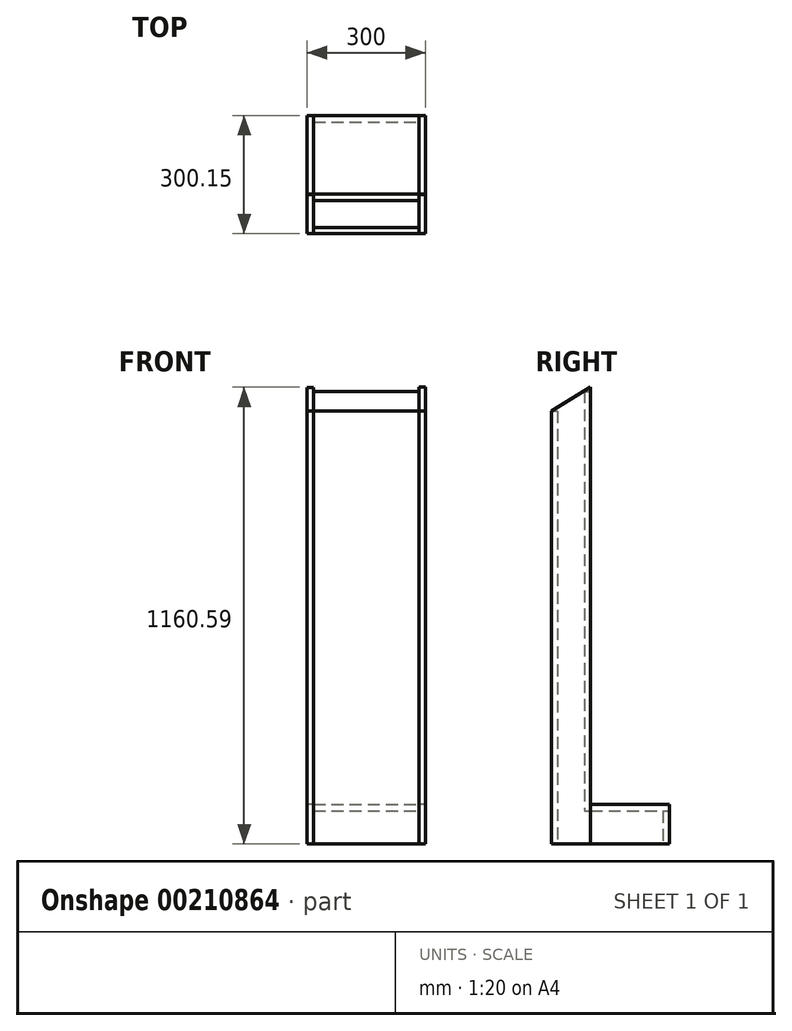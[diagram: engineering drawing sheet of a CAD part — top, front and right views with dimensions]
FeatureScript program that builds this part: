
annotation { "Feature Type Name" : "Feature", "Feature Type Description" : "" }
export const myFeature = defineFeature(function(context is Context, id is Id, definition is map)
    precondition{}
    {
        {
            var Q0;
            Q0=qCreatedBy(makeId("Front.planeOp"),FACE);
            cPlane(context, id + "F0", {"entities" : qUnion([Q0]), "cplaneType" : CPlaneType.OFFSET, "offset" : 100 * mm, "width" : 150 * mm, "height" : 150 * mm});
        }
        {
            var Q0;
            Q0=qCreatedBy(id+"F0.planeOp",FACE);
            var sketch = newSketch(context, id + "F1", { "sketchPlane" : qUnion([Q0])});
            skLineSegment(sketch, "E0.bottom", {"start": v(134, 550) * mm, "end": v(-134, 550) * mm});
            skLineSegment(sketch, "E0.top", {"start": v(134, -550) * mm, "end": v(-134, -550) * mm});
            skLineSegment(sketch, "E0.left", {"start": v(134, 550) * mm, "end": v(134, -550) * mm});
            skLineSegment(sketch, "E0.right", {"start": v(-134, 550) * mm, "end": v(-134, -550) * mm});
            skPoint(sketch, "E0.middle", {"position": v(0, 0) * mm});
            skSolve(sketch);
        }
        {
            var Q0;
            Q0 = qSketchRegion(id + "F1", true);
            extrude(context, id + "F2", {"entities" : qUnion([Q0]), "depth" : 16 * mm});
        }
        {
            var Q0;
            Q0=qCreatedBy(makeId("Front.planeOp"),FACE);
            cPlane(context, id + "F3", {"entities" : qUnion([Q0]), "cplaneType" : CPlaneType.OFFSET, "offset" : 100 * mm, "oppositeDirection" : true, "width" : 150 * mm, "height" : 150 * mm});
        }
        {
            var Q0;
            Q0=qCreatedBy(id+"F3.planeOp",FACE);
            var sketch = newSketch(context, id + "F4", { "sketchPlane" : qUnion([Q0])});
            skLineSegment(sketch, "E1.bottom", {"start": v(-134, 533) * mm, "end": v(134, 533) * mm});
            skLineSegment(sketch, "E1.top", {"start": v(-134, -533) * mm, "end": v(134, -533) * mm});
            skLineSegment(sketch, "E1.left", {"start": v(-134, 533) * mm, "end": v(-134, -533) * mm});
            skLineSegment(sketch, "E1.right", {"start": v(134, 533) * mm, "end": v(134, -533) * mm});
            skPoint(sketch, "E1.middle", {"position": v(0, 0) * mm});
            skSolve(sketch);
        }
        {
            var Q0;
            Q0=makeQuery(id+"F4.imprint","IMPRINT",FACE,{"disambiguationData":[TD([[makeQuery(id+"F4.imprint","IMPRINT",EDGE,{"derivedFrom":sQuery(id+"F4.wireOp",EDGE,"E1.bottom")}),-1.0]])]});
            extrude(context, id + "F5", {"entities" : qUnion([Q0]), "depth" : 16 * mm});
        }
        {
            var Q0;
            Q0=qCreatedBy(makeId("Right.planeOp"),FACE);
            cPlane(context, id + "F6", {"entities" : qUnion([Q0]), "cplaneType" : CPlaneType.OFFSET, "offset" : 100 * mm, "width" : 150 * mm, "height" : 150 * mm});
        }
        {
            var Q0;
            Q0=qCreatedBy(id+"F6.planeOp",FACE);
            var sketch = newSketch(context, id + "F7", { "sketchPlane" : qUnion([Q0])});
            skLineSegment(sketch, "E2.bottom", {"start": v(82.35, 1083.55) * mm, "end": v(-17.65, 1083.55) * mm});
            skLineSegment(sketch, "E2.top", {"start": v(82.35, -76.45) * mm, "end": v(-17.65, -76.45) * mm});
            skLineSegment(sketch, "E2.left", {"start": v(82.35, 1083.55) * mm, "end": v(82.35, -76.45) * mm});
            skLineSegment(sketch, "E2.right", {"start": v(-17.65, 1083.55) * mm, "end": v(-17.65, -76.45) * mm});
            skPoint(sketch, "E2.middle", {"position": v(32.35, 503.55) * mm});
            skSolve(sketch);
        }
        {
            var Q0;
            Q0 = qSketchRegion(id + "F7", true);
            extrude(context, id + "F8", {"entities" : qUnion([Q0]), "depth" : 16 * mm});
        }
        {
            var Q0;
            Q0=qCreatedBy(makeId("Right.planeOp"),FACE);
            cPlane(context, id + "F9", {"entities" : qUnion([Q0]), "cplaneType" : CPlaneType.OFFSET, "offset" : 100 * mm, "oppositeDirection" : true, "width" : 150 * mm, "height" : 150 * mm});
        }
        {
            var Q0;
            Q0=qCreatedBy(id+"F9.planeOp",FACE);
            var sketch = newSketch(context, id + "F10", { "sketchPlane" : qUnion([Q0])});
            skLineSegment(sketch, "E3.bottom", {"start": v(-50, 580) * mm, "end": v(50, 580) * mm});
            skLineSegment(sketch, "E3.top", {"start": v(-50, -580) * mm, "end": v(50, -580) * mm});
            skLineSegment(sketch, "E3.left", {"start": v(-50, 580) * mm, "end": v(-50, -580) * mm});
            skLineSegment(sketch, "E3.right", {"start": v(50, 580) * mm, "end": v(50, -580) * mm});
            skPoint(sketch, "E3.middle", {"position": v(0, 0) * mm});
            skSolve(sketch);
        }
        {
            var Q0;
            Q0=makeQuery(id+"F10.imprint","IMPRINT",FACE,{"disambiguationData":[TD([[makeQuery(id+"F10.imprint","IMPRINT",EDGE,{"derivedFrom":sQuery(id+"F10.wireOp",EDGE,"E3.bottom")}),-1.0]])]});
            extrude(context, id + "F11", {"entities" : qUnion([Q0]), "depth" : 16 * mm});
        }
        {
            var Q0;
            Q0=makeQuery(id+"F2.opExtrude","SWEPT_BODY",BODY,{"disambiguationData":[OSD([sQuery(id+"F1.wireOp",EDGE,"E0.bottom"),sQuery(id+"F1.wireOp",EDGE,"E0.top"),sQuery(id+"F1.wireOp",EDGE,"E0.left"),sQuery(id+"F1.wireOp",EDGE,"E0.right")])]});
            transform(context, id + "F12", {"entities" : qUnion([Q0]), "transformType" : TransformType.TRANSLATION_3D, "dx" : 0 * mm, "dy" : 50 * mm, "dz" : 0 * mm, "makeCopy" : false});
        }
        {
            var Q0;
            Q0=makeQuery(id+"F5.opExtrude","SWEPT_BODY",BODY,{"disambiguationData":[OSD([sQuery(id+"F4.wireOp",EDGE,"E1.bottom"),sQuery(id+"F4.wireOp",EDGE,"E1.top"),sQuery(id+"F4.wireOp",EDGE,"E1.left"),sQuery(id+"F4.wireOp",EDGE,"E1.right")])]});
            transform(context, id + "F13", {"entities" : qUnion([Q0]), "transformType" : TransformType.TRANSLATION_3D, "dx" : 0 * mm, "dy" : -33.8 * mm, "dz" : 0 * mm, "makeCopy" : false});
        }
        {
            var Q0;
            Q0=makeQuery(id+"F11.opExtrude","SWEPT_BODY",BODY,{"disambiguationData":[OSD([sQuery(id+"F10.wireOp",EDGE,"E3.bottom"),sQuery(id+"F10.wireOp",EDGE,"E3.top"),sQuery(id+"F10.wireOp",EDGE,"E3.left"),sQuery(id+"F10.wireOp",EDGE,"E3.right")])]});
            transform(context, id + "F14", {"entities" : qUnion([Q0]), "transformType" : TransformType.TRANSLATION_3D, "dx" : -50 * mm, "dy" : 0 * mm, "dz" : 0 * mm, "makeCopy" : false});
        }
        {
            var Q0;
            Q0=makeQuery(id+"F8.opExtrude","SWEPT_BODY",BODY,{"disambiguationData":[OSD([sQuery(id+"F7.wireOp",EDGE,"E2.bottom"),sQuery(id+"F7.wireOp",EDGE,"E2.top"),sQuery(id+"F7.wireOp",EDGE,"E2.left"),sQuery(id+"F7.wireOp",EDGE,"E2.right")])]});
            transform(context, id + "F15", {"entities" : qUnion([Q0]), "transformType" : TransformType.TRANSLATION_3D, "dx" : 34 * mm, "dy" : -32.4 * mm, "dz" : 0 * mm, "makeCopy" : false});
        }
        {
            var Q0;
            Q0=makeQuery(id+"F8.opExtrude","SWEPT_BODY",BODY,{"disambiguationData":[OSD([sQuery(id+"F7.wireOp",EDGE,"E2.bottom"),sQuery(id+"F7.wireOp",EDGE,"E2.top"),sQuery(id+"F7.wireOp",EDGE,"E2.left"),sQuery(id+"F7.wireOp",EDGE,"E2.right")])]});
            transform(context, id + "F16", {"entities" : qUnion([Q0]), "transformType" : TransformType.TRANSLATION_3D, "dx" : 0 * mm, "dy" : 0 * mm, "dz" : -473 * mm, "makeCopy" : false});
        }
        {
            var Q0;
            Q0=makeQuery(id+"F11.opExtrude","SWEPT_BODY",BODY,{"disambiguationData":[OSD([sQuery(id+"F10.wireOp",EDGE,"E3.bottom"),sQuery(id+"F10.wireOp",EDGE,"E3.top"),sQuery(id+"F10.wireOp",EDGE,"E3.left"),sQuery(id+"F10.wireOp",EDGE,"E3.right")])]});
            transform(context, id + "F17", {"entities" : qUnion([Q0]), "transformType" : TransformType.TRANSLATION_3D, "dx" : 16 * mm, "dy" : 0 * mm, "dz" : 0 * mm, "makeCopy" : false});
        }
        {
            var Q0;
            Q0=makeQuery(id+"F8.opExtrude","SWEPT_BODY",BODY,{"disambiguationData":[OSD([sQuery(id+"F7.wireOp",EDGE,"E2.bottom"),sQuery(id+"F7.wireOp",EDGE,"E2.top"),sQuery(id+"F7.wireOp",EDGE,"E2.left"),sQuery(id+"F7.wireOp",EDGE,"E2.right")])]});
            transform(context, id + "F18", {"entities" : qUnion([Q0]), "transformType" : TransformType.TRANSLATION_3D, "dx" : -16 * mm, "dy" : 0 * mm, "dz" : 0 * mm, "makeCopy" : false});
        }
        {
            var Q0;
            Q0=makeQuery(id+"F11.opExtrude","SWEPT_BODY",BODY,{"disambiguationData":[OSD([sQuery(id+"F10.wireOp",EDGE,"E3.bottom"),sQuery(id+"F10.wireOp",EDGE,"E3.top"),sQuery(id+"F10.wireOp",EDGE,"E3.left"),sQuery(id+"F10.wireOp",EDGE,"E3.right")])]});
            transform(context, id + "F19", {"entities" : qUnion([Q0]), "transformType" : TransformType.TRANSLATION_3D, "dx" : 0 * mm, "dy" : 0 * mm, "dz" : 30 * mm, "makeCopy" : false});
        }
        {
            var Q0;
            Q0=makeQuery(id+"F8.opExtrude","SWEPT_BODY",BODY,{"disambiguationData":[OSD([sQuery(id+"F7.wireOp",EDGE,"E2.bottom"),sQuery(id+"F7.wireOp",EDGE,"E2.top"),sQuery(id+"F7.wireOp",EDGE,"E2.left"),sQuery(id+"F7.wireOp",EDGE,"E2.right")])]});
            transform(context, id + "F20", {"entities" : qUnion([Q0]), "transformType" : TransformType.TRANSLATION_3D, "dx" : 16 * mm, "dy" : 0 * mm, "dz" : 0 * mm, "makeCopy" : false});
        }
        {
            var Q0;
            Q0=makeQuery(id+"F11.opExtrude","SWEPT_BODY",BODY,{"disambiguationData":[OSD([sQuery(id+"F10.wireOp",EDGE,"E3.bottom"),sQuery(id+"F10.wireOp",EDGE,"E3.top"),sQuery(id+"F10.wireOp",EDGE,"E3.left"),sQuery(id+"F10.wireOp",EDGE,"E3.right")])]});
            transform(context, id + "F21", {"entities" : qUnion([Q0]), "transformType" : TransformType.TRANSLATION_3D, "dx" : -16 * mm, "dy" : 0 * mm, "dz" : 0 * mm, "makeCopy" : false});
        }
        {
            var Q0;
            Q0=makeQuery(id+"F5.opExtrude","SWEPT_BODY",BODY,{"disambiguationData":[OSD([sQuery(id+"F4.wireOp",EDGE,"E1.bottom"),sQuery(id+"F4.wireOp",EDGE,"E1.top"),sQuery(id+"F4.wireOp",EDGE,"E1.left"),sQuery(id+"F4.wireOp",EDGE,"E1.right")])]});
            transform(context, id + "F22", {"entities" : qUnion([Q0]), "transformType" : TransformType.TRANSLATION_3D, "dx" : 0 * mm, "dy" : -16 * mm, "dz" : 0 * mm, "makeCopy" : false});
        }
        {
            var Q0;
            Q0=makeQuery(id+"F5.opExtrude","SWEPT_BODY",BODY,{"disambiguationData":[OSD([sQuery(id+"F4.wireOp",EDGE,"E1.bottom"),sQuery(id+"F4.wireOp",EDGE,"E1.top"),sQuery(id+"F4.wireOp",EDGE,"E1.left"),sQuery(id+"F4.wireOp",EDGE,"E1.right")])]});
            transform(context, id + "F23", {"entities" : qUnion([Q0]), "transformType" : TransformType.TRANSLATION_3D, "dx" : 0 * mm, "dy" : 0 * mm, "dz" : 0 * mm, "makeCopy" : false});
        }
        {
            var Q0;
            Q0=makeQuery(id+"F2.opExtrude","SWEPT_BODY",BODY,{"disambiguationData":[OSD([sQuery(id+"F1.wireOp",EDGE,"E0.bottom"),sQuery(id+"F1.wireOp",EDGE,"E0.top"),sQuery(id+"F1.wireOp",EDGE,"E0.left"),sQuery(id+"F1.wireOp",EDGE,"E0.right")])]});
            transform(context, id + "F24", {"entities" : qUnion([Q0]), "transformType" : TransformType.TRANSLATION_3D, "dx" : 0 * mm, "dy" : 16 * mm, "dz" : 0 * mm, "makeCopy" : false});
        }
        {
            var Q0;
            Q0=makeQuery(id+"F5.opExtrude","SWEPT_BODY",BODY,{"disambiguationData":[OSD([sQuery(id+"F4.wireOp",EDGE,"E1.bottom"),sQuery(id+"F4.wireOp",EDGE,"E1.top"),sQuery(id+"F4.wireOp",EDGE,"E1.left"),sQuery(id+"F4.wireOp",EDGE,"E1.right")])]});
            transform(context, id + "F25", {"entities" : qUnion([Q0]), "transformType" : TransformType.TRANSLATION_3D, "dx" : 0 * mm, "dy" : -0.2 * mm, "dz" : 0 * mm, "makeCopy" : false});
        }
        {
            var Q0;
            Q0=makeQuery(id+"F11.opExtrude","SWEPT_EDGE",EDGE,{"disambiguationData":[OSD([sQuery(id+"F10.wireOp",EDGE,"E3.bottom"),sQuery(id+"F10.wireOp",EDGE,"E3.left")])]});
            chamfer(context, id + "F26", {"entities" : qUnion([Q0]), "chamferType" : ChamferType.OFFSET_ANGLE, "width" : 60 * mm, "oppositeDirection" : false, "angle" : 59 * degree, "tangentPropagation" : true});
        }
        {
            var Q0;
            Q0=makeQuery(id+"F8.opExtrude","SWEPT_EDGE",EDGE,{"disambiguationData":[OSD([sQuery(id+"F7.wireOp",EDGE,"E2.bottom"),sQuery(id+"F7.wireOp",EDGE,"E2.right")])]});
            chamfer(context, id + "F27", {"entities" : qUnion([Q0]), "chamferType" : ChamferType.OFFSET_ANGLE, "width" : 60 * mm, "oppositeDirection" : false, "angle" : 59 * degree, "tangentPropagation" : true});
        }
        {
            var Q0;
            Q0=makeQuery(id+"F5.opExtrude","SWEPT_BODY",BODY,{"disambiguationData":[OSD([sQuery(id+"F4.wireOp",EDGE,"E1.bottom"),sQuery(id+"F4.wireOp",EDGE,"E1.top"),sQuery(id+"F4.wireOp",EDGE,"E1.left"),sQuery(id+"F4.wireOp",EDGE,"E1.right")])]});
            transform(context, id + "F28", {"entities" : qUnion([Q0]), "transformType" : TransformType.TRANSLATION_3D, "dx" : 0 * mm, "dy" : 0 * mm, "dz" : 66 * mm, "makeCopy" : false});
        }
        {
            var Q0;
            Q0=qCreatedBy(makeId("Right.planeOp"),FACE);
            cPlane(context, id + "F29", {"entities" : qUnion([Q0]), "cplaneType" : CPlaneType.OFFSET, "offset" : 200 * mm, "oppositeDirection" : true, "width" : 150 * mm, "height" : 150 * mm});
        }
        {
            var Q0;
            Q0=qCreatedBy(id+"F29.planeOp",FACE);
            var sketch = newSketch(context, id + "F30", { "sketchPlane" : qUnion([Q0])});
            skLineSegment(sketch, "E4.bottom", {"start": v(100, -50) * mm, "end": v(-100, -50) * mm});
            skLineSegment(sketch, "E4.top", {"start": v(100, 50) * mm, "end": v(-100, 50) * mm});
            skLineSegment(sketch, "E4.left", {"start": v(100, -50) * mm, "end": v(100, 50) * mm});
            skLineSegment(sketch, "E4.right", {"start": v(-100, -50) * mm, "end": v(-100, 50) * mm});
            skPoint(sketch, "E4.middle", {"position": v(0, 0) * mm});
            skSolve(sketch);
        }
        {
            var Q0;
            Q0 = qSketchRegion(id + "F30", true);
            extrude(context, id + "F31", {"entities" : qUnion([Q0]), "depth" : 16 * mm});
        }
        {
            var Q0;
            Q0=makeQuery(id+"F31.opExtrude","SWEPT_BODY",BODY,{"disambiguationData":[OSD([sQuery(id+"F30.wireOp",EDGE,"E4.bottom"),sQuery(id+"F30.wireOp",EDGE,"E4.top"),sQuery(id+"F30.wireOp",EDGE,"E4.left"),sQuery(id+"F30.wireOp",EDGE,"E4.right")])]});
            transform(context, id + "F32", {"entities" : qUnion([Q0]), "transformType" : TransformType.TRANSLATION_3D, "dx" : 0 * mm, "dy" : 150.1 * mm, "dz" : -500 * mm, "makeCopy" : false});
        }
        {
            var Q0;
            Q0=makeQuery(id+"F31.opExtrude","SWEPT_BODY",BODY,{"disambiguationData":[OSD([sQuery(id+"F30.wireOp",EDGE,"E4.bottom"),sQuery(id+"F30.wireOp",EDGE,"E4.top"),sQuery(id+"F30.wireOp",EDGE,"E4.left"),sQuery(id+"F30.wireOp",EDGE,"E4.right")])]});
            transform(context, id + "F33", {"entities" : qUnion([Q0]), "transformType" : TransformType.TRANSLATION_3D, "dx" : 50 * mm, "dy" : 0 * mm, "dz" : 0 * mm, "makeCopy" : false});
        }
        {
            var Q0;
            Q0=qCreatedBy(makeId("Right.planeOp"),FACE);
            cPlane(context, id + "F34", {"entities" : qUnion([Q0]), "cplaneType" : CPlaneType.OFFSET, "offset" : 200 * mm, "width" : 150 * mm, "height" : 150 * mm});
        }
        {
            var Q0;
            Q0=qCreatedBy(id+"F34.planeOp",FACE);
            var sketch = newSketch(context, id + "F35", { "sketchPlane" : qUnion([Q0])});
            skLineSegment(sketch, "E5.bottom", {"start": v(75.3, 49.56) * mm, "end": v(-124.7, 49.56) * mm});
            skLineSegment(sketch, "E5.top", {"start": v(75.3, -50.44) * mm, "end": v(-124.7, -50.44) * mm});
            skLineSegment(sketch, "E5.left", {"start": v(75.3, 49.56) * mm, "end": v(75.3, -50.44) * mm});
            skLineSegment(sketch, "E5.right", {"start": v(-124.7, 49.56) * mm, "end": v(-124.7, -50.44) * mm});
            skPoint(sketch, "E5.middle", {"position": v(-24.7, -0.44) * mm});
            skSolve(sketch);
        }
        {
            var Q0;
            Q0=makeQuery(id+"F35.imprint","IMPRINT",FACE,{"disambiguationData":[TD([[makeQuery(id+"F35.imprint","IMPRINT",EDGE,{"derivedFrom":sQuery(id+"F35.wireOp",EDGE,"E5.bottom")}),1.0]])]});
            extrude(context, id + "F36", {"entities" : qUnion([Q0]), "depth" : 16 * mm});
        }
        {
            var Q0;
            Q0=makeQuery(id+"F36.opExtrude","SWEPT_BODY",BODY,{"disambiguationData":[OSD([sQuery(id+"F35.wireOp",EDGE,"E5.bottom"),sQuery(id+"F35.wireOp",EDGE,"E5.top"),sQuery(id+"F35.wireOp",EDGE,"E5.left"),sQuery(id+"F35.wireOp",EDGE,"E5.right")])]});
            transform(context, id + "F37", {"entities" : qUnion([Q0]), "transformType" : TransformType.TRANSLATION_3D, "dx" : 0 * mm, "dy" : 174.8 * mm, "dz" : -499.6 * mm, "makeCopy" : false});
        }
        {
            var Q0;
            Q0=makeQuery(id+"F36.opExtrude","SWEPT_BODY",BODY,{"disambiguationData":[OSD([sQuery(id+"F35.wireOp",EDGE,"E5.bottom"),sQuery(id+"F35.wireOp",EDGE,"E5.top"),sQuery(id+"F35.wireOp",EDGE,"E5.left"),sQuery(id+"F35.wireOp",EDGE,"E5.right")])]});
            transform(context, id + "F38", {"entities" : qUnion([Q0]), "transformType" : TransformType.TRANSLATION_3D, "dx" : -66 * mm, "dy" : 0 * mm, "dz" : 0 * mm, "makeCopy" : false});
        }
        {
            var Q0;
            Q0=qCreatedBy(makeId("Top.planeOp"),FACE);
            cPlane(context, id + "F39", {"entities" : qUnion([Q0]), "cplaneType" : CPlaneType.OFFSET, "offset" : 500 * mm, "oppositeDirection" : true, "width" : 150 * mm, "height" : 150 * mm});
        }
        {
            var Q0;
            Q0=qCreatedBy(id+"F39.planeOp",FACE);
            var sketch = newSketch(context, id + "F40", { "sketchPlane" : qUnion([Q0])});
            skLineSegment(sketch, "E6.bottom", {"start": v(-134, 49.94) * mm, "end": v(134, 49.94) * mm});
            skLineSegment(sketch, "E6.top", {"start": v(-134, 249.94) * mm, "end": v(134, 249.94) * mm});
            skLineSegment(sketch, "E6.left", {"start": v(-134, 49.94) * mm, "end": v(-134, 249.94) * mm});
            skLineSegment(sketch, "E6.right", {"start": v(134, 49.94) * mm, "end": v(134, 249.94) * mm});
            skSolve(sketch);
        }
        {
            var Q0;
            Q0=makeQuery(id+"F40.imprint","IMPRINT",FACE,{"disambiguationData":[TD([[makeQuery(id+"F40.imprint","IMPRINT",EDGE,{"derivedFrom":sQuery(id+"F40.wireOp",EDGE,"E6.bottom")}),1.0]])]});
            extrude(context, id + "F41", {"entities" : qUnion([Q0]), "depth" : 16 * mm});
        }
        {
            var Q0;
            Q0=makeQuery(id+"F41.opExtrude","SWEPT_BODY",BODY,{"disambiguationData":[OSD([sQuery(id+"F40.wireOp",EDGE,"E6.bottom"),sQuery(id+"F40.wireOp",EDGE,"E6.top"),sQuery(id+"F40.wireOp",EDGE,"E6.left"),sQuery(id+"F40.wireOp",EDGE,"E6.right")])]});
            transform(context, id + "F42", {"entities" : qUnion([Q0]), "transformType" : TransformType.TRANSLATION_3D, "dx" : 0 * mm, "dy" : 0 * mm, "dz" : 34 * mm, "makeCopy" : false});
        }
        {
            var Q0;
            Q0=makeQuery(id+"F5.opExtrude","SWEPT_BODY",BODY,{"disambiguationData":[OSD([sQuery(id+"F4.wireOp",EDGE,"E1.bottom"),sQuery(id+"F4.wireOp",EDGE,"E1.top"),sQuery(id+"F4.wireOp",EDGE,"E1.left"),sQuery(id+"F4.wireOp",EDGE,"E1.right")])]});
            transform(context, id + "F43", {"entities" : qUnion([Q0]), "transformType" : TransformType.TRANSLATION_3D, "dx" : 0 * mm, "dy" : 0 * mm, "dz" : 1 * mm, "makeCopy" : false});
        }
        {
            var Q0;
            Q0=qCreatedBy(makeId("Front.planeOp"),FACE);
            cPlane(context, id + "F44", {"entities" : qUnion([Q0]), "cplaneType" : CPlaneType.OFFSET, "offset" : 200 * mm, "oppositeDirection" : true, "width" : 150 * mm, "height" : 150 * mm});
        }
        {
            var Q0;
            Q0=qCreatedBy(id+"F44.planeOp",FACE);
            var sketch = newSketch(context, id + "F45", { "sketchPlane" : qUnion([Q0])});
            skLineSegment(sketch, "E7.bottom", {"start": v(-134, 42) * mm, "end": v(134, 42) * mm});
            skLineSegment(sketch, "E7.top", {"start": v(-134, -42) * mm, "end": v(134, -42) * mm});
            skLineSegment(sketch, "E7.left", {"start": v(-134, 42) * mm, "end": v(-134, -42) * mm});
            skLineSegment(sketch, "E7.right", {"start": v(134, 42) * mm, "end": v(134, -42) * mm});
            skPoint(sketch, "E7.middle", {"position": v(0, 0) * mm});
            skSolve(sketch);
        }
        {
            var Q0;
            Q0=makeQuery(id+"F45.imprint","IMPRINT",FACE,{"disambiguationData":[TD([[makeQuery(id+"F45.imprint","IMPRINT",EDGE,{"derivedFrom":sQuery(id+"F45.wireOp",EDGE,"E7.bottom")}),-1.0]])]});
            extrude(context, id + "F46", {"entities" : qUnion([Q0]), "depth" : 16 * mm});
        }
        {
            var Q0;
            Q0=makeQuery(id+"F46.opExtrude","SWEPT_BODY",BODY,{"disambiguationData":[OSD([sQuery(id+"F45.wireOp",EDGE,"E7.bottom"),sQuery(id+"F45.wireOp",EDGE,"E7.top"),sQuery(id+"F45.wireOp",EDGE,"E7.left"),sQuery(id+"F45.wireOp",EDGE,"E7.right")])]});
            transform(context, id + "F47", {"entities" : qUnion([Q0]), "transformType" : TransformType.TRANSLATION_3D, "dx" : 0 * mm, "dy" : 50 * mm, "dz" : -508 * mm, "makeCopy" : false});
        }
    });
